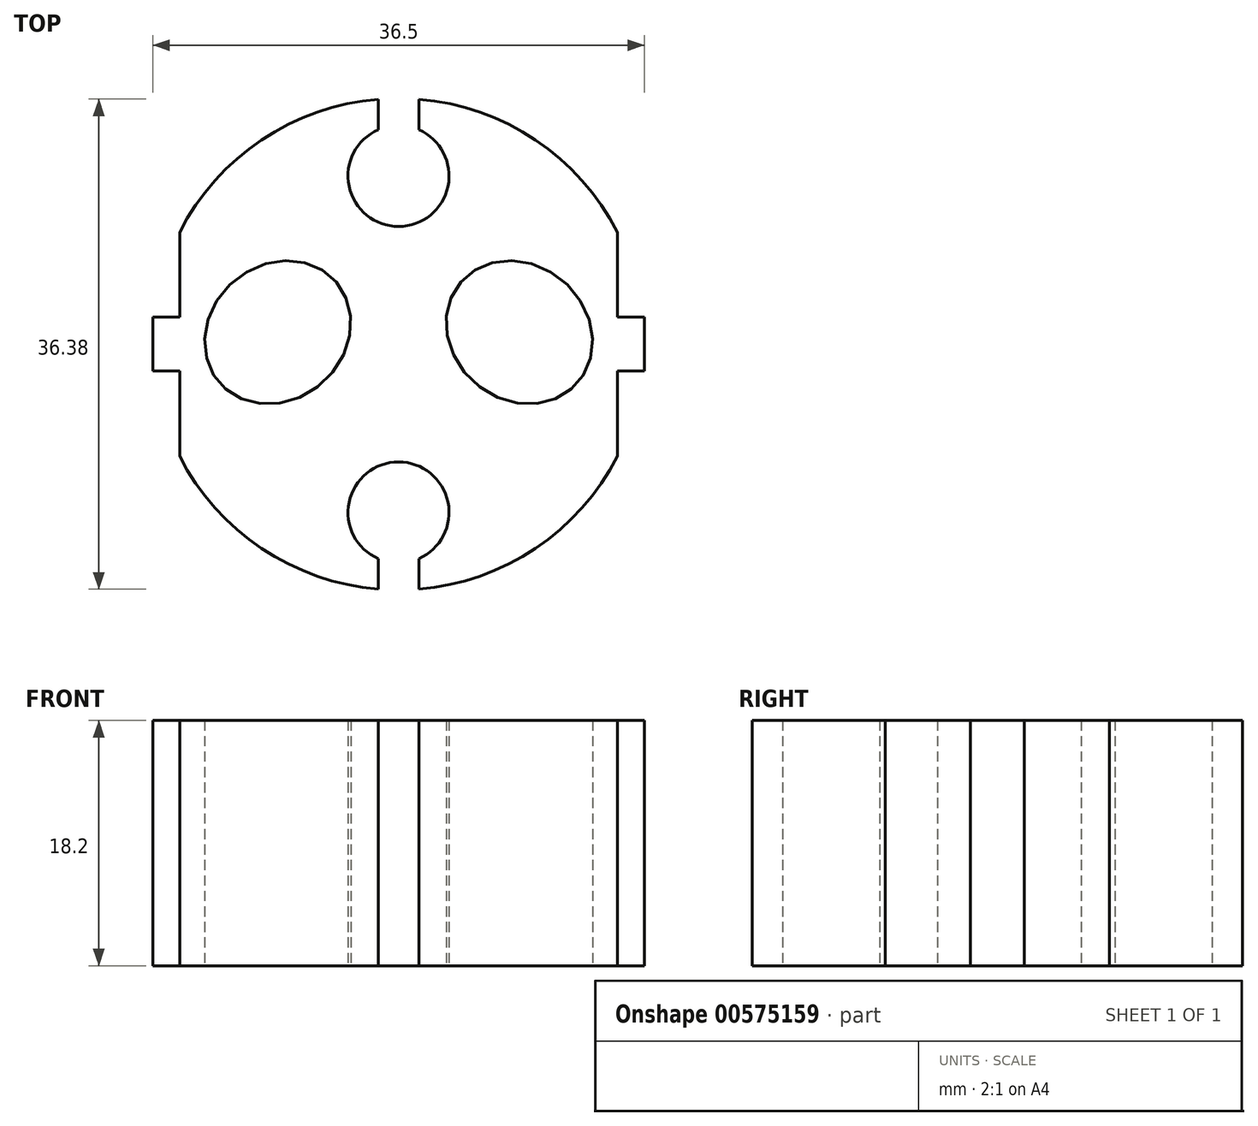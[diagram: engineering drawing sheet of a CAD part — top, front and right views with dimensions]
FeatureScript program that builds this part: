
annotation { "Feature Type Name" : "Feature", "Feature Type Description" : "" }
export const myFeature = defineFeature(function(context is Context, id is Id, definition is map)
    precondition{}
    {
        {
            var Q0;
            Q0=qCreatedBy(makeId("Top.planeOp"),FACE);
            var sketch = newSketch(context, id + "F0", { "sketchPlane" : qUnion([Q0])});
            skArc(sketch, "E0", {"start": v(16.25, 8.3) * mm, "mid": v(10.16, 15.16) * mm, "end": v(1.5, 18.19) * mm});
            skCircle(sketch, "E1", {"center": v(0, 0) * mm, "radius": 16.25 * mm, "construction": true});
            skLineSegment(sketch, "E2", {"start": v(0, 20.44) * mm, "end": v(0, -20.48) * mm, "construction": true});
            skLineSegment(sketch, "E3", {"start": v(-16.25, 8.3) * mm, "end": v(-16.25, 2) * mm});
            skLineSegment(sketch, "E4.MirrorCS", {"start": v(16.25, 8.3) * mm, "end": v(16.25, 2) * mm});
            skPoint(sketch, "E5.orphan", {"position": v(-16.25, 25.95) * mm});
            skPoint(sketch, "E6.orphan", {"position": v(16.25, 25.95) * mm});
            skPoint(sketch, "E7.orphan", {"position": v(16.25, -32.27) * mm});
            skPoint(sketch, "E8.orphan", {"position": v(-16.25, -32.27) * mm});
            skArc(sketch, "E9.trimOffspring", {"start": v(-16.25, -8.3) * mm, "mid": v(-10.16, -15.16) * mm, "end": v(-1.5, -18.19) * mm});
            skLineSegment(sketch, "E10", {"start": v(-25.91, 0) * mm, "end": v(23.22, 0) * mm, "construction": true});
            skPoint(sketch, "E10.startSnap0", {"position": v(-16.25, 0) * mm});
            skLineSegment(sketch, "E11", {"start": v(-16.25, 0) * mm, "end": v(-18.25, 0) * mm});
            skLineSegment(sketch, "E12", {"start": v(-18.25, 0) * mm, "end": v(-18.25, -2) * mm});
            skLineSegment(sketch, "E13", {"start": v(-18.25, -2) * mm, "end": v(-16.25, -2) * mm});
            skLineSegment(sketch, "E14.MirrorCS", {"start": v(-18.25, 0) * mm, "end": v(-18.25, 2) * mm});
            skLineSegment(sketch, "E15.MirrorCS", {"start": v(-18.25, 2) * mm, "end": v(-16.25, 2) * mm});
            skLineSegment(sketch, "E16.MirrorCS", {"start": v(18.25, -2) * mm, "end": v(16.25, -2) * mm});
            skLineSegment(sketch, "E17.MirrorCS", {"start": v(18.25, 0) * mm, "end": v(18.25, -2) * mm});
            skLineSegment(sketch, "E18.MirrorCS", {"start": v(18.25, 2) * mm, "end": v(16.25, 2) * mm});
            skLineSegment(sketch, "E19.MirrorCS", {"start": v(18.25, 0) * mm, "end": v(18.25, 2) * mm});
            skLineSegment(sketch, "E20.trimOffspring", {"start": v(-16.25, -2) * mm, "end": v(-16.25, -8.3) * mm});
            skLineSegment(sketch, "E21.trimOffspring", {"start": v(16.25, -2) * mm, "end": v(16.25, -8.3) * mm});
            skEllipse(sketch, "E22", {"center": v(-8.97, 0.88) * mm, "majorRadius": 5.73 * mm, "minorRadius": 5 * mm, "majorAxis": v(0.76, 0.65)});
            skEllipse(sketch, "E23.MirrorC", {"center": v(8.97, 0.88) * mm, "majorRadius": 5.73 * mm, "minorRadius": 5 * mm, "majorAxis": v(-0.76, 0.65)});
            skCircle(sketch, "E24", {"center": v(-10, 0) * mm, "radius": 2.5 * mm, "construction": true});
            skCircle(sketch, "E25", {"center": v(10, 0) * mm, "radius": 2.5 * mm, "construction": true});
            skLineSegment(sketch, "E26", {"start": v(-10, 0) * mm, "end": v(0, 12.49) * mm, "construction": true});
            skLineSegment(sketch, "E27", {"start": v(0, 12.49) * mm, "end": v(10, 0) * mm, "construction": true});
            skArc(sketch, "E28", {"start": v(-1.5, 15.93) * mm, "mid": v(0, 8.74) * mm, "end": v(1.5, 15.93) * mm});
            skLineSegment(sketch, "E29", {"start": v(-1.5, 18.19) * mm, "end": v(-1.5, 15.93) * mm});
            skLineSegment(sketch, "E30.MirrorCS", {"start": v(1.5, 18.19) * mm, "end": v(1.5, 15.93) * mm});
            skArc(sketch, "E31.trimOffspring", {"start": v(-1.5, 18.19) * mm, "mid": v(-10.16, 15.16) * mm, "end": v(-16.25, 8.3) * mm});
            skLineSegment(sketch, "E32.MirrorCS", {"start": v(1.5, -18.19) * mm, "end": v(1.5, -15.93) * mm});
            skLineSegment(sketch, "E33.MirrorCS", {"start": v(-1.5, -18.19) * mm, "end": v(-1.5, -15.93) * mm});
            skArc(sketch, "E34.MirrorCS", {"start": v(-1.5, -15.93) * mm, "mid": v(0, -8.74) * mm, "end": v(1.5, -15.93) * mm});
            skArc(sketch, "E35.trimOffspring", {"start": v(1.5, -18.19) * mm, "mid": v(10.16, -15.16) * mm, "end": v(16.25, -8.3) * mm});
            skSolve(sketch);
        }
        {
            var Q0;
            Q0=makeQuery(id+"F0.imprint","IMPRINT",FACE,{"disambiguationData":[TD([[makeQuery(id+"F0.imprint","IMPRINT",EDGE,{"derivedFrom":sQuery(id+"F0.wireOp",EDGE,"E0")}),1.0]])]});
            extrude(context, id + "F1", {"entities" : qUnion([Q0]), "depth" : 18.2 * mm, "offsetDistance" : 25 * mm});
        }
    });
